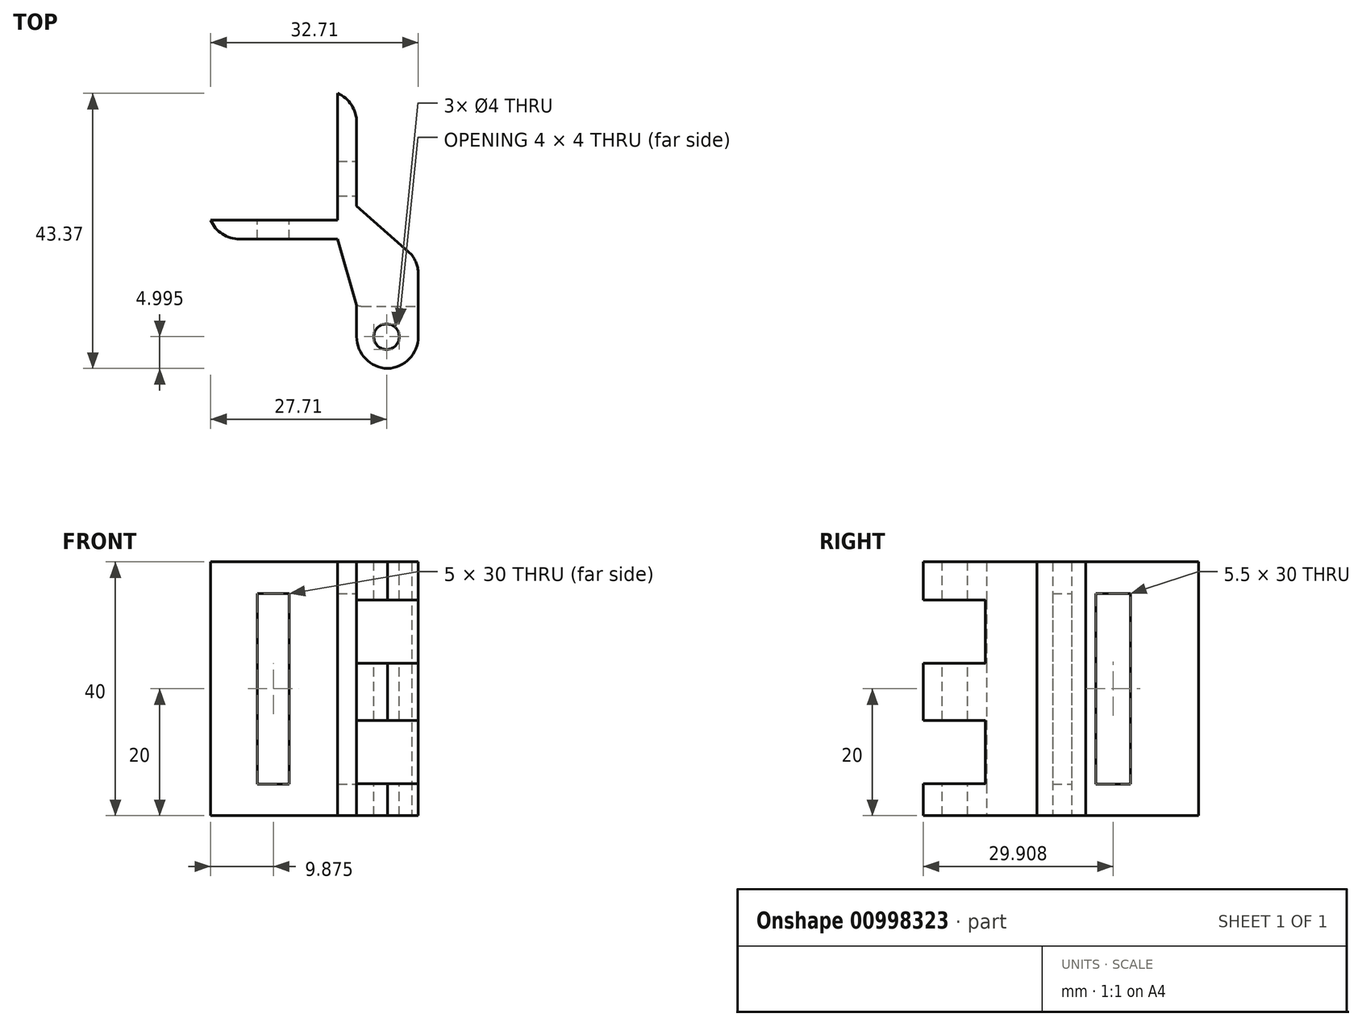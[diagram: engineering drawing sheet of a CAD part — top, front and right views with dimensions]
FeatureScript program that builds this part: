
annotation { "Feature Type Name" : "Feature", "Feature Type Description" : "" }
export const myFeature = defineFeature(function(context is Context, id is Id, definition is map)
    precondition{}
    {
        {
            var Q0;
            Q0=qCreatedBy(makeId("Top.planeOp"),FACE);
            var sketch = newSketch(context, id + "F0", { "sketchPlane" : qUnion([Q0])});
            skLineSegment(sketch, "E0", {"start": v(-8.95, -9.81) * mm, "end": v(1.05, -9.81) * mm});
            skLineSegment(sketch, "E1", {"start": v(1.05, -9.81) * mm, "end": v(1.05, 8.08) * mm});
            skLineSegment(sketch, "E2", {"start": v(1.05, 8.08) * mm, "end": v(0, 8.08) * mm});
            skLineSegment(sketch, "E3", {"start": v(0, 8.08) * mm, "end": v(-8.66, 15.8) * mm});
            skLineSegment(sketch, "E4", {"start": v(-8.66, 15.8) * mm, "end": v(-8.66, 33.56) * mm});
            skLineSegment(sketch, "E5", {"start": v(-8.66, 33.56) * mm, "end": v(-11.66, 33.56) * mm});
            skLineSegment(sketch, "E6", {"start": v(-11.66, 33.56) * mm, "end": v(-11.66, 13.56) * mm});
            skLineSegment(sketch, "E7", {"start": v(-11.66, 13.56) * mm, "end": v(-31.66, 13.56) * mm});
            skLineSegment(sketch, "E8", {"start": v(-31.66, 13.56) * mm, "end": v(-31.66, 10.56) * mm});
            skLineSegment(sketch, "E9", {"start": v(-31.66, 10.56) * mm, "end": v(-11.66, 10.56) * mm});
            skLineSegment(sketch, "E10", {"start": v(-11.66, 10.56) * mm, "end": v(-8.66, 0.19) * mm});
            skLineSegment(sketch, "E11", {"start": v(-8.66, 0.19) * mm, "end": v(-8.66, -9.81) * mm});
            skSolve(sketch);
        }
        {
            var Q0;
            {var subQ0=sQuery(id+"F0.wireOp",EDGE,"E1");Q0=makeQuery(id+"F0.imprint","IMPRINT",FACE,{"disambiguationData":[TD([[makeQuery(id+"F0.imprint","IMPRINT",EDGE,{"derivedFrom":subQ0}),1.0]])]});}
            extrude(context, id + "F1", {"entities" : qUnion([Q0]), "depth" : 40 * mm, "offsetDistance" : 25 * mm});
        }
        {
            var Q0;
            Q0=makeQuery(id+"F1.opExtrude","SWEPT_FACE",FACE,{"disambiguationData":[OSD([sQuery(id+"F0.wireOp",EDGE,"E4")])]});
            var sketch = newSketch(context, id + "F2", { "sketchPlane" : qUnion([Q0])});
            skLineSegment(sketch, "E12.bottom", {"start": v(17.35, 35) * mm, "end": v(22.85, 35) * mm});
            skLineSegment(sketch, "E12.top", {"start": v(17.35, 5) * mm, "end": v(22.85, 5) * mm});
            skLineSegment(sketch, "E12.left", {"start": v(17.35, 35) * mm, "end": v(17.35, 5) * mm});
            skLineSegment(sketch, "E12.right", {"start": v(22.85, 35) * mm, "end": v(22.85, 5) * mm});
            skSolve(sketch);
        }
        {
            var Q0;
            Q0=makeQuery(id+"F2.imprint","IMPRINT",FACE,{"disambiguationData":[TD([[makeQuery(id+"F2.imprint","IMPRINT",EDGE,{"derivedFrom":sQuery(id+"F2.wireOp",EDGE,"E12.bottom")}),-1.0]])]});
            extrude(context, id + "F3", {"entities" : qUnion([Q0]), "operationType" : NewBodyOperationType.REMOVE, "oppositeDirection" : true, "depth" : 50 * mm, "offsetDistance" : 25 * mm});
        }
        {
            var Q0;
            Q0=makeQuery(id+"F1.opExtrude","SWEPT_FACE",FACE,{"disambiguationData":[OSD([sQuery(id+"F0.wireOp",EDGE,"E7")])]});
            var sketch = newSketch(context, id + "F4", { "sketchPlane" : qUnion([Q0])});
            skLineSegment(sketch, "E13.bottom", {"start": v(19.28, 35) * mm, "end": v(24.28, 35) * mm});
            skLineSegment(sketch, "E13.top", {"start": v(19.28, 5) * mm, "end": v(24.28, 5) * mm});
            skLineSegment(sketch, "E13.left", {"start": v(19.28, 35) * mm, "end": v(19.28, 5) * mm});
            skLineSegment(sketch, "E13.right", {"start": v(24.28, 35) * mm, "end": v(24.28, 5) * mm});
            skSolve(sketch);
        }
        {
            var Q0;
            Q0=makeQuery(id+"F4.imprint","IMPRINT",FACE,{"disambiguationData":[TD([[makeQuery(id+"F4.imprint","IMPRINT",EDGE,{"derivedFrom":sQuery(id+"F4.wireOp",EDGE,"E13.bottom")}),-1.0]])]});
            extrude(context, id + "F5", {"entities" : qUnion([Q0]), "operationType" : NewBodyOperationType.REMOVE, "oppositeDirection" : true, "depth" : 25 * mm, "offsetDistance" : 25 * mm});
        }
        {
            var Q0;
            Q0=makeQuery(id+"F1.opExtrude","SWEPT_FACE",FACE,{"disambiguationData":[OSD([sQuery(id+"F0.wireOp",EDGE,"E1")])]});
            var sketch = newSketch(context, id + "F6", { "sketchPlane" : qUnion([Q0])});
            skLineSegment(sketch, "E14.bottom", {"start": v(-12.54, 34.02) * mm, "end": v(0, 34.02) * mm});
            skLineSegment(sketch, "E14.top", {"start": v(-12.54, 24.02) * mm, "end": v(0, 24.02) * mm});
            skLineSegment(sketch, "E14.left", {"start": v(-12.54, 34.02) * mm, "end": v(-12.54, 24.02) * mm});
            skLineSegment(sketch, "E14.right", {"start": v(0, 34.02) * mm, "end": v(0, 24.02) * mm});
            skLineSegment(sketch, "E15.bottom", {"start": v(-12.54, 15.02) * mm, "end": v(0, 15.02) * mm});
            skLineSegment(sketch, "E15.top", {"start": v(-12.54, 5.02) * mm, "end": v(0, 5.02) * mm});
            skLineSegment(sketch, "E15.left", {"start": v(-12.54, 15.02) * mm, "end": v(-12.54, 5.02) * mm});
            skLineSegment(sketch, "E15.right", {"start": v(0, 15.02) * mm, "end": v(0, 5.02) * mm});
            skSolve(sketch);
        }
        {
            var Q0;
            Q0=makeQuery(id+"F6.imprint","IMPRINT",FACE,{"disambiguationData":[TD([[makeQuery(id+"F6.imprint","IMPRINT",EDGE,{"derivedFrom":sQuery(id+"F6.wireOp",EDGE,"E14.bottom")}),-1.0]])]});
            var Q1;
            Q1=makeQuery(id+"F6.imprint","IMPRINT",FACE,{"disambiguationData":[TD([[makeQuery(id+"F6.imprint","IMPRINT",EDGE,{"derivedFrom":sQuery(id+"F6.wireOp",EDGE,"E15.bottom")}),-1.0]])]});
            extrude(context, id + "F7", {"entities" : qUnion([Q0, Q1]), "operationType" : NewBodyOperationType.REMOVE, "oppositeDirection" : true, "depth" : 25 * mm, "offsetDistance" : 25 * mm});
        }
        {
            var Q0;
            Q0=makeQuery(id+"F1.opExtrude","CAP_FACE",FACE,{"disambiguationData":[OSD([sQuery(id+"F0.wireOp",EDGE,"E0"),sQuery(id+"F0.wireOp",EDGE,"E1"),sQuery(id+"F0.wireOp",EDGE,"E2"),sQuery(id+"F0.wireOp",EDGE,"E3"),sQuery(id+"F0.wireOp",EDGE,"E4"),sQuery(id+"F0.wireOp",EDGE,"E5"),sQuery(id+"F0.wireOp",EDGE,"E6"),sQuery(id+"F0.wireOp",EDGE,"E7"),sQuery(id+"F0.wireOp",EDGE,"E8"),sQuery(id+"F0.wireOp",EDGE,"E9"),sQuery(id+"F0.wireOp",EDGE,"E10"),sQuery(id+"F0.wireOp",EDGE,"E11")])],"isStart":false});
            var sketch = newSketch(context, id + "F8", { "sketchPlane" : qUnion([Q0])});
            skCircle(sketch, "E16", {"center": v(-3.95, -4.81) * mm, "radius": 2 * mm});
            skSolve(sketch);
        }
        {
            var Q0;
            Q0=makeQuery(id+"F8.imprint","IMPRINT",FACE,{"disambiguationData":[TD([[makeQuery(id+"F8.imprint","IMPRINT",EDGE,{"derivedFrom":sQuery(id+"F8.wireOp",EDGE,"E16")}),1.0]])]});
            extrude(context, id + "F9", {"entities" : qUnion([Q0]), "operationType" : NewBodyOperationType.REMOVE, "oppositeDirection" : true, "depth" : 50 * mm, "offsetDistance" : 25 * mm});
        }
        {
            var Q0;
            {var subQ0=sQuery(id+"F0.wireOp",EDGE,"E0");var subQ1=sQuery(id+"F0.wireOp",EDGE,"E1");Q0=makeQuery(id+"F7.boolean.opBoolean","SPLIT",EDGE,{"disambiguationData":[TD([makeQuery(id+"F7.opExtrude","SWEPT_FACE",FACE,{"disambiguationData":[OSD([sQuery(id+"F6.wireOp",EDGE,"E14.bottom")])]})])],"derivedFrom":makeQuery(id+"F1.opExtrude","SWEPT_EDGE",EDGE,{"disambiguationData":[OSD([subQ0,subQ1])]})});}
            var Q1;
            {var subQ0=sQuery(id+"F0.wireOp",EDGE,"E0");var subQ1=sQuery(id+"F0.wireOp",EDGE,"E11");Q1=makeQuery(id+"F7.boolean.opBoolean","SPLIT",EDGE,{"disambiguationData":[TD([makeQuery(id+"F7.opExtrude","SWEPT_FACE",FACE,{"disambiguationData":[OSD([sQuery(id+"F6.wireOp",EDGE,"E14.bottom")])]})])],"derivedFrom":makeQuery(id+"F1.opExtrude","SWEPT_EDGE",EDGE,{"disambiguationData":[OSD([subQ0,subQ1])]})});}
            var Q2;
            {var subQ0=sQuery(id+"F0.wireOp",EDGE,"E0");var subQ1=sQuery(id+"F0.wireOp",EDGE,"E1");Q2=makeQuery(id+"F7.boolean.opBoolean","SPLIT",EDGE,{"disambiguationData":[TD([makeQuery(id+"F7.opExtrude","SWEPT_FACE",FACE,{"disambiguationData":[OSD([sQuery(id+"F6.wireOp",EDGE,"E14.top")])]})])],"derivedFrom":makeQuery(id+"F1.opExtrude","SWEPT_EDGE",EDGE,{"disambiguationData":[OSD([subQ0,subQ1])]})});}
            var Q3;
            {var subQ0=sQuery(id+"F0.wireOp",EDGE,"E0");var subQ1=sQuery(id+"F0.wireOp",EDGE,"E11");Q3=makeQuery(id+"F7.boolean.opBoolean","SPLIT",EDGE,{"disambiguationData":[TD([makeQuery(id+"F7.opExtrude","SWEPT_FACE",FACE,{"disambiguationData":[OSD([sQuery(id+"F6.wireOp",EDGE,"E14.top")])]})])],"derivedFrom":makeQuery(id+"F1.opExtrude","SWEPT_EDGE",EDGE,{"disambiguationData":[OSD([subQ0,subQ1])]})});}
            var Q4;
            {var subQ0=sQuery(id+"F0.wireOp",EDGE,"E0");var subQ1=sQuery(id+"F0.wireOp",EDGE,"E1");Q4=makeQuery(id+"F7.boolean.opBoolean","SPLIT",EDGE,{"disambiguationData":[TD([makeQuery(id+"F7.opExtrude","SWEPT_FACE",FACE,{"disambiguationData":[OSD([sQuery(id+"F6.wireOp",EDGE,"E15.top")])]})])],"derivedFrom":makeQuery(id+"F1.opExtrude","SWEPT_EDGE",EDGE,{"disambiguationData":[OSD([subQ0,subQ1])]})});}
            var Q5;
            {var subQ0=sQuery(id+"F0.wireOp",EDGE,"E0");var subQ1=sQuery(id+"F0.wireOp",EDGE,"E11");Q5=makeQuery(id+"F7.boolean.opBoolean","SPLIT",EDGE,{"disambiguationData":[TD([makeQuery(id+"F7.opExtrude","SWEPT_FACE",FACE,{"disambiguationData":[OSD([sQuery(id+"F6.wireOp",EDGE,"E15.top")])]})])],"derivedFrom":makeQuery(id+"F1.opExtrude","SWEPT_EDGE",EDGE,{"disambiguationData":[OSD([subQ0,subQ1])]})});}
            var Q6;
            Q6=makeQuery(id+"F1.opExtrude","SWEPT_EDGE",EDGE,{"disambiguationData":[OSD([sQuery(id+"F0.wireOp",EDGE,"E1"),sQuery(id+"F0.wireOp",EDGE,"E2")])]});
            var Q7;
            Q7=makeQuery(id+"F1.opExtrude","SWEPT_EDGE",EDGE,{"disambiguationData":[OSD([sQuery(id+"F0.wireOp",EDGE,"E4"),sQuery(id+"F0.wireOp",EDGE,"E5")])]});
            var Q8;
            Q8=makeQuery(id+"F1.opExtrude","SWEPT_EDGE",EDGE,{"disambiguationData":[OSD([sQuery(id+"F0.wireOp",EDGE,"E8"),sQuery(id+"F0.wireOp",EDGE,"E9")])]});
            fillet(context, id + "F10", {"entities" : qUnion([Q0, Q1, Q2, Q3, Q4, Q5, Q6, Q7, Q8]), "radius" : 5 * mm, "tangentPropagation" : true, "allowEdgeOverflow" : false});
        }
        {
            var Q0;
            Q0=makeQuery(id+"F7.boolean.opBoolean","COPY",EDGE,{"derivedFrom":makeQuery(id+"F7.opExtrude","CAP_EDGE",EDGE,{"disambiguationData":[OSD([sQuery(id+"F6.wireOp",EDGE,"E14.right")])],"isStart":true})});
            var Q1;
            Q1=makeQuery(id+"F7.boolean.opBoolean","COPY",EDGE,{"derivedFrom":makeQuery(id+"F7.opExtrude","CAP_EDGE",EDGE,{"disambiguationData":[OSD([sQuery(id+"F6.wireOp",EDGE,"E15.right")])],"isStart":true})});
            var Q2;
            Q2=makeQuery(id+"F7.boolean.opBoolean","INTERSECT",EDGE,{"derivedFrom":[makeQuery(id+"F1.opExtrude","SWEPT_FACE",FACE,{"disambiguationData":[OSD([sQuery(id+"F0.wireOp",EDGE,"E11")])]}),makeQuery(id+"F7.opExtrude","SWEPT_FACE",FACE,{"disambiguationData":[OSD([sQuery(id+"F6.wireOp",EDGE,"E15.right")])]})]});
            var Q3;
            Q3=makeQuery(id+"F7.boolean.opBoolean","INTERSECT",EDGE,{"derivedFrom":[makeQuery(id+"F1.opExtrude","SWEPT_FACE",FACE,{"disambiguationData":[OSD([sQuery(id+"F0.wireOp",EDGE,"E11")])]}),makeQuery(id+"F7.opExtrude","SWEPT_FACE",FACE,{"disambiguationData":[OSD([sQuery(id+"F6.wireOp",EDGE,"E14.right")])]})]});
            fillet(context, id + "F11", {"entities" : qUnion([Q0, Q1, Q2, Q3]), "radius" : 2 * mm, "tangentPropagation" : true, "allowEdgeOverflow" : false});
        }
    });
